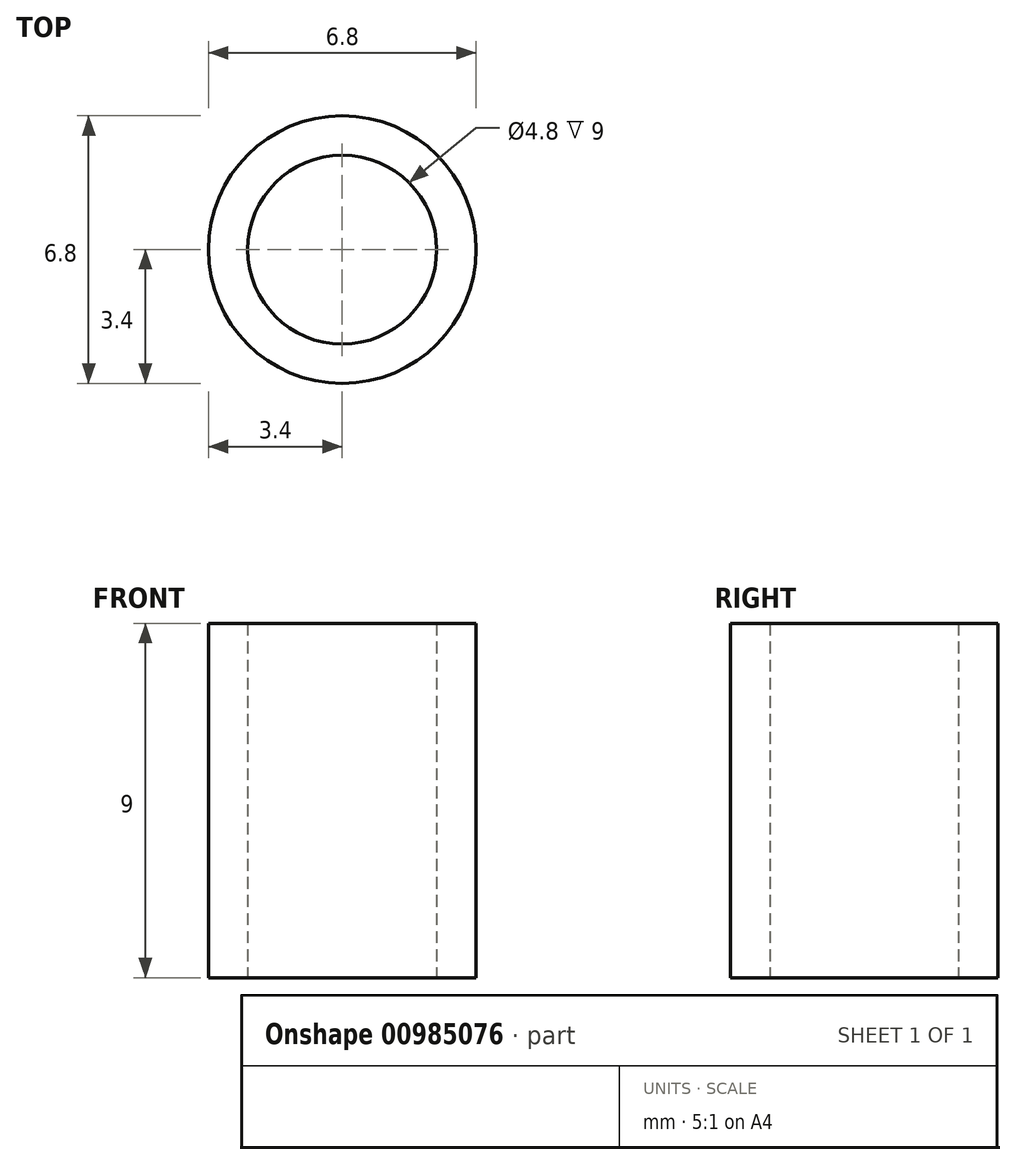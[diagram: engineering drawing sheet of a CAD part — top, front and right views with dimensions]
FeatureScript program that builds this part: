
annotation { "Feature Type Name" : "Feature", "Feature Type Description" : "" }
export const myFeature = defineFeature(function(context is Context, id is Id, definition is map)
    precondition{}
    {
        {
            var Q0;
            Q0=qCreatedBy(makeId("Top.planeOp"),FACE);
            var sketch = newSketch(context, id + "F0", { "sketchPlane" : qUnion([Q0])});
            skCircle(sketch, "E0", {"center": v(0, 0) * mm, "radius": 3.4 * mm});
            skCircle(sketch, "E1", {"center": v(0, 0) * mm, "radius": 2.4 * mm});
            skSolve(sketch);
        }
        {
            var Q0;
            Q0 = qSketchRegion(id + "F0", true);
            extrude(context, id + "F1", {"entities" : qUnion([Q0]), "depth" : 9 * mm, "offsetDistance" : 25 * mm});
        }
    });
